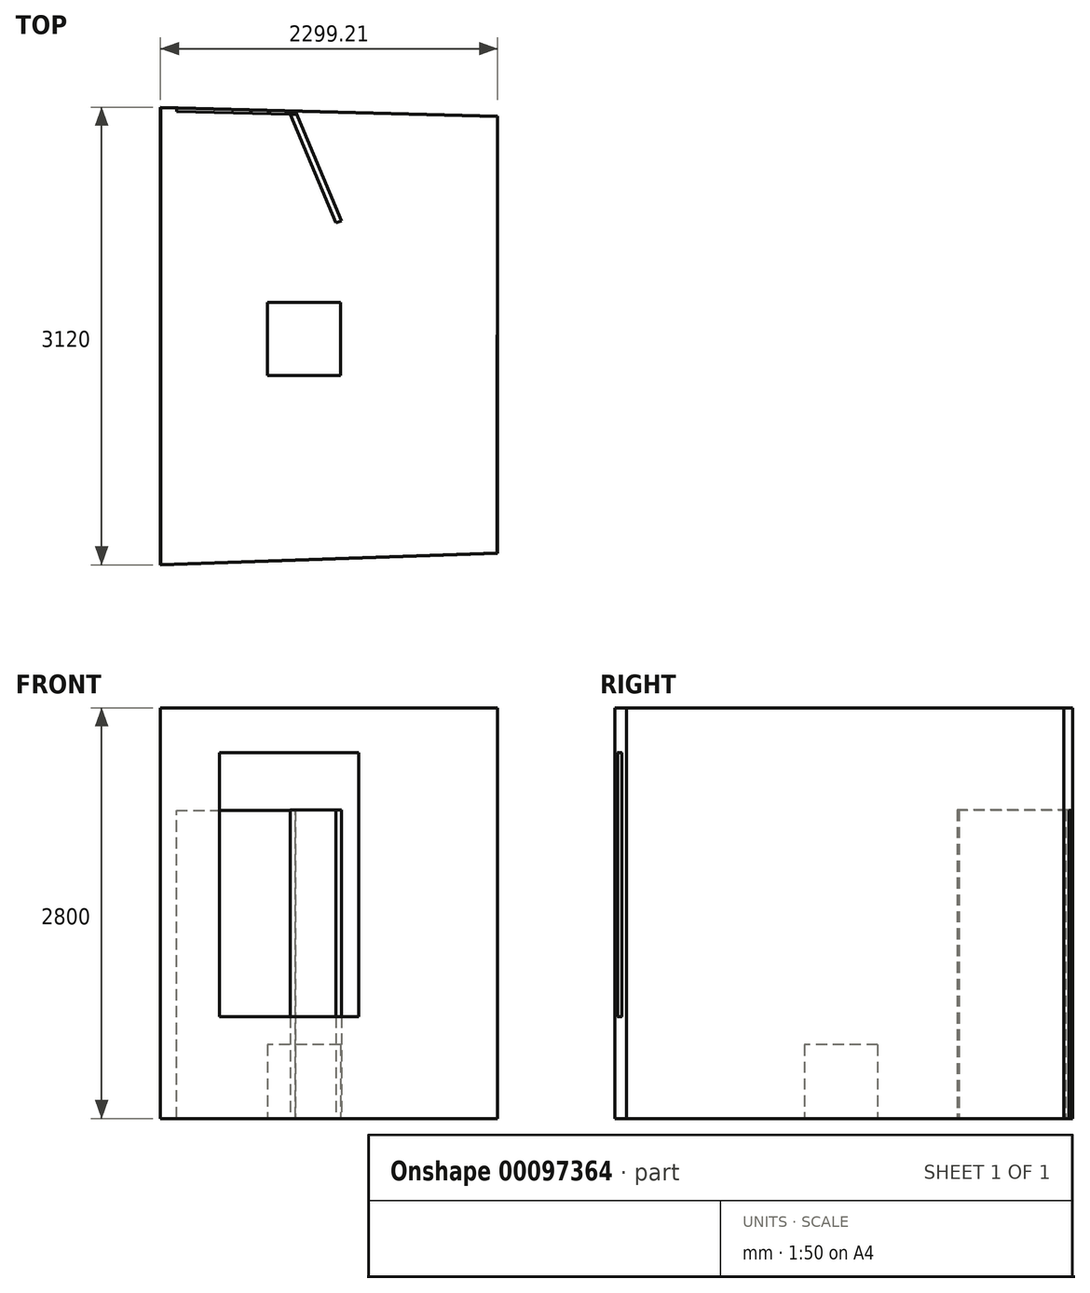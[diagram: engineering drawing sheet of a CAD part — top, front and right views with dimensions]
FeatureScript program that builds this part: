
annotation { "Feature Type Name" : "Feature", "Feature Type Description" : "" }
export const myFeature = defineFeature(function(context is Context, id is Id, definition is map)
    precondition{}
    {
        {
            var Q0;
            Q0=qCreatedBy(makeId("Top.planeOp"),FACE);
            var sketch = newSketch(context, id + "F0", { "sketchPlane" : qUnion([Q0])});
            skLineSegment(sketch, "E0", {"start": v(0, -3120) * mm, "end": v(2298.62, -3040.36) * mm});
            skLineSegment(sketch, "E1", {"start": v(0, 0) * mm, "end": v(2299.2, -60.36) * mm, "construction": true});
            skLineSegment(sketch, "E2", {"start": v(0, 0) * mm, "end": v(0, -3120) * mm});
            skLineSegment(sketch, "E3", {"start": v(2299.2, -60.36) * mm, "end": v(2298.62, -3040.36) * mm});
            skLineSegment(sketch, "E4", {"start": v(0, 0) * mm, "end": v(110, -2.89) * mm});
            skArc(sketch, "E5", {"start": v(110, -2.89) * mm, "mid": v(339.58, -589.54) * mm, "end": v(920, -834.43) * mm});
            skLineSegment(sketch, "E6", {"start": v(920, -24.15) * mm, "end": v(920, -834.43) * mm});
            skLineSegment(sketch, "E7", {"start": v(920, -24.15) * mm, "end": v(979.2, -25.7) * mm});
            skLineSegment(sketch, "E8", {"start": v(979.2, -25.7) * mm, "end": v(2299.2, -60.36) * mm});
            skLineSegment(sketch, "E9", {"start": v(110, -2.89) * mm, "end": v(920, -24.15) * mm});
            skSolve(sketch);
        }
        {
            var Q0;
            Q0=makeQuery(id+"F0.imprint","IMPRINT",FACE,{"disambiguationData":[TD([[makeQuery(id+"F0.imprint","IMPRINT",EDGE,{"derivedFrom":sQuery(id+"F0.wireOp",EDGE,"E0")}),1.0]])]});
            var Q1;
            Q1=makeQuery(id+"F0.imprint","IMPRINT",FACE,{"disambiguationData":[TD([[makeQuery(id+"F0.imprint","IMPRINT",EDGE,{"derivedFrom":sQuery(id+"F0.wireOp",EDGE,"E5")}),1.0]])]});
            var Q2;
            Q2=sQuery(id+"F0.wireOp",EDGE,"E2");
            var Q3;
            Q3=sQuery(id+"F0.wireOp",EDGE,"E3");
            var Q4;
            Q4=sQuery(id+"F0.wireOp",EDGE,"E0");
            var Q5;
            Q5=sQuery(id+"F0.wireOp",EDGE,"E8");
            var Q6;
            Q6=sQuery(id+"F0.wireOp",EDGE,"E4");
            var Q7;
            Q7=sQuery(id+"F0.wireOp",EDGE,"E7");
            extrude(context, id + "F1", {"entities" : qUnion([Q0, Q1]), "surfaceEntities" : qUnion([Q2, Q3, Q4, Q5, Q6, Q7]), "depth" : 2800 * mm});
        }
        {
            var Q0;
            Q0=makeQuery(id+"F1.opExtrude","SWEPT_FACE",FACE,{"disambiguationData":[OSD([sQuery(id+"F0.wireOp",EDGE,"E4"),sQuery(id+"F0.wireOp",EDGE,"E7"),sQuery(id+"F0.wireOp",EDGE,"E8"),sQuery(id+"F0.wireOp",EDGE,"E9")])]});
            var sketch = newSketch(context, id + "F2", { "sketchPlane" : qUnion([Q0])});
            skLineSegment(sketch, "E10.bottom", {"start": v(-110.04, 0) * mm, "end": v(-920.32, 0) * mm, "construction": true});
            skLineSegment(sketch, "E10.top", {"start": v(-110.04, 2100) * mm, "end": v(-920.32, 2100) * mm});
            skLineSegment(sketch, "E10.left", {"start": v(-110.04, 0) * mm, "end": v(-110.04, 2100) * mm});
            skLineSegment(sketch, "E10.right", {"start": v(-920.32, 0) * mm, "end": v(-920.32, 2100) * mm});
            skLineSegment(sketch, "E11.0", {"start": v(0, 2800) * mm, "end": v(-2300, 2800) * mm});
            skLineSegment(sketch, "E12.0.0", {"start": v(-2377.63, 0) * mm, "end": v(-2300, 0) * mm});
            skLineSegment(sketch, "E12.0.1", {"start": v(-2300, 0) * mm, "end": v(-2300, 2800) * mm});
            skLineSegment(sketch, "E12.0.2", {"start": v(-2300, 2800) * mm, "end": v(-2377.63, 2800) * mm});
            skLineSegment(sketch, "E12.0.3", {"start": v(-2377.63, 2800) * mm, "end": v(-2377.63, 0) * mm});
            skLineSegment(sketch, "E13.0", {"start": v(0, 2800) * mm, "end": v(0, 0) * mm});
            skLineSegment(sketch, "E14", {"start": v(-2300, 0) * mm, "end": v(-920.32, 0) * mm});
            skLineSegment(sketch, "E15", {"start": v(-110.04, 0) * mm, "end": v(0, 0) * mm});
            skSolve(sketch);
        }
        {
            var Q0;
            Q0=makeQuery(id+"F1.opExtrude","CAP_FACE",FACE,{"disambiguationData":[OSD([sQuery(id+"F0.wireOp",EDGE,"E0"),sQuery(id+"F0.wireOp",EDGE,"E2"),sQuery(id+"F0.wireOp",EDGE,"E3"),sQuery(id+"F0.wireOp",EDGE,"E4"),sQuery(id+"F0.wireOp",EDGE,"E7"),sQuery(id+"F0.wireOp",EDGE,"E8"),sQuery(id+"F0.wireOp",EDGE,"E9")])],"isStart":false});
            shell(context, id + "F3", {"entities" : qUnion([Q0]), "thickness" : 2.5 * mm});
        }
        {
            var Q0;
            Q0=makeQuery(id+"F2.imprint","IMPRINT",FACE,{"disambiguationData":[TD([[makeQuery(id+"F2.imprint","IMPRINT",EDGE,{"derivedFrom":sQuery(id+"F2.wireOp",EDGE,"E10.top")}),1.0]])]});
            extrude(context, id + "F4", {"entities" : qUnion([Q0]), "operationType" : NewBodyOperationType.REMOVE, "oppositeDirection" : true, "depth" : 25 * mm});
        }
        {
            var Q0;
            Q0=makeQuery(id+"F1.opExtrude","SWEPT_FACE",FACE,{"disambiguationData":[OSD([sQuery(id+"F0.wireOp",EDGE,"E0")])]});
            var sketch = newSketch(context, id + "F5", { "sketchPlane" : qUnion([Q0])});
            skLineSegment(sketch, "E16.bottom", {"start": v(1244.56, 2494.42) * mm, "end": v(294.56, 2494.42) * mm});
            skLineSegment(sketch, "E16.top", {"start": v(1244.56, 694.42) * mm, "end": v(294.56, 694.42) * mm});
            skLineSegment(sketch, "E16.left", {"start": v(1244.56, 2494.42) * mm, "end": v(1244.56, 694.42) * mm});
            skLineSegment(sketch, "E16.right", {"start": v(294.56, 2494.42) * mm, "end": v(294.56, 694.42) * mm});
            skPoint(sketch, "E16.middle", {"position": v(769.56, 1594.42) * mm});
            skSolve(sketch);
        }
        {
            var Q0;
            Q0=makeQuery(id+"F5.imprint","IMPRINT",FACE,{"disambiguationData":[TD([[makeQuery(id+"F5.imprint","IMPRINT",EDGE,{"derivedFrom":sQuery(id+"F5.wireOp",EDGE,"E16.bottom")}),1.0]])]});
            extrude(context, id + "F6", {"entities" : qUnion([Q0]), "operationType" : NewBodyOperationType.REMOVE, "oppositeDirection" : true, "depth" : 25 * mm});
        }
        {
            var Q0;
            Q0=makeQuery(id+"F3.opShell","OFFSET_FACE",FACE,{"disambiguationData":[OSD([sQuery(id+"F0.wireOp",EDGE,"E0"),sQuery(id+"F0.wireOp",EDGE,"E2"),sQuery(id+"F0.wireOp",EDGE,"E3"),sQuery(id+"F0.wireOp",EDGE,"E4"),sQuery(id+"F0.wireOp",EDGE,"E7"),sQuery(id+"F0.wireOp",EDGE,"E8"),sQuery(id+"F0.wireOp",EDGE,"E9")])]});
            var sketch = newSketch(context, id + "F7", { "sketchPlane" : qUnion([Q0])});
            skLineSegment(sketch, "E17", {"start": v(919.93, -26.65) * mm, "end": v(1233.39, -773.26) * mm});
            skLineSegment(sketch, "E18", {"start": v(1233.39, -773.26) * mm, "end": v(1196.5, -788.74) * mm});
            skLineSegment(sketch, "E19", {"start": v(1196.5, -788.74) * mm, "end": v(882.95, -41.9) * mm});
            skLineSegment(sketch, "E20", {"start": v(882.95, -41.9) * mm, "end": v(919.93, -26.65) * mm});
            skSolve(sketch);
        }
        {
            var Q0;
            Q0=makeQuery(id+"F7.imprint","IMPRINT",FACE,{"disambiguationData":[TD([[makeQuery(id+"F7.imprint","IMPRINT",EDGE,{"derivedFrom":sQuery(id+"F7.wireOp",EDGE,"E17")}),-1.0]])]});
            extrude(context, id + "F8", {"entities" : qUnion([Q0]), "depth" : 2100 * mm});
        }
        {
            var Q0;
            Q0=makeQuery(id+"F3.opShell","OFFSET_FACE",FACE,{"disambiguationData":[OSD([sQuery(id+"F0.wireOp",EDGE,"E0"),sQuery(id+"F0.wireOp",EDGE,"E2"),sQuery(id+"F0.wireOp",EDGE,"E3"),sQuery(id+"F0.wireOp",EDGE,"E4"),sQuery(id+"F0.wireOp",EDGE,"E7"),sQuery(id+"F0.wireOp",EDGE,"E8"),sQuery(id+"F0.wireOp",EDGE,"E9")])]});
            var sketch = newSketch(context, id + "F9", { "sketchPlane" : qUnion([Q0])});
            skLineSegment(sketch, "E21.bottom", {"start": v(1228.15, -1329.48) * mm, "end": v(728.15, -1329.48) * mm});
            skLineSegment(sketch, "E21.top", {"start": v(1228.15, -1829.48) * mm, "end": v(728.15, -1829.48) * mm});
            skLineSegment(sketch, "E21.left", {"start": v(1228.15, -1329.48) * mm, "end": v(1228.15, -1829.48) * mm});
            skLineSegment(sketch, "E21.right", {"start": v(728.15, -1329.48) * mm, "end": v(728.15, -1829.48) * mm});
            skPoint(sketch, "E21.middle", {"position": v(978.15, -1579.48) * mm});
            skSolve(sketch);
        }
        {
            var Q0;
            Q0=makeQuery(id+"F9.imprint","IMPRINT",FACE,{"disambiguationData":[TD([[makeQuery(id+"F9.imprint","IMPRINT",EDGE,{"derivedFrom":sQuery(id+"F9.wireOp",EDGE,"E21.bottom")}),1.0]])]});
            extrude(context, id + "F10", {"entities" : qUnion([Q0]), "depth" : 500 * mm});
        }
    });
